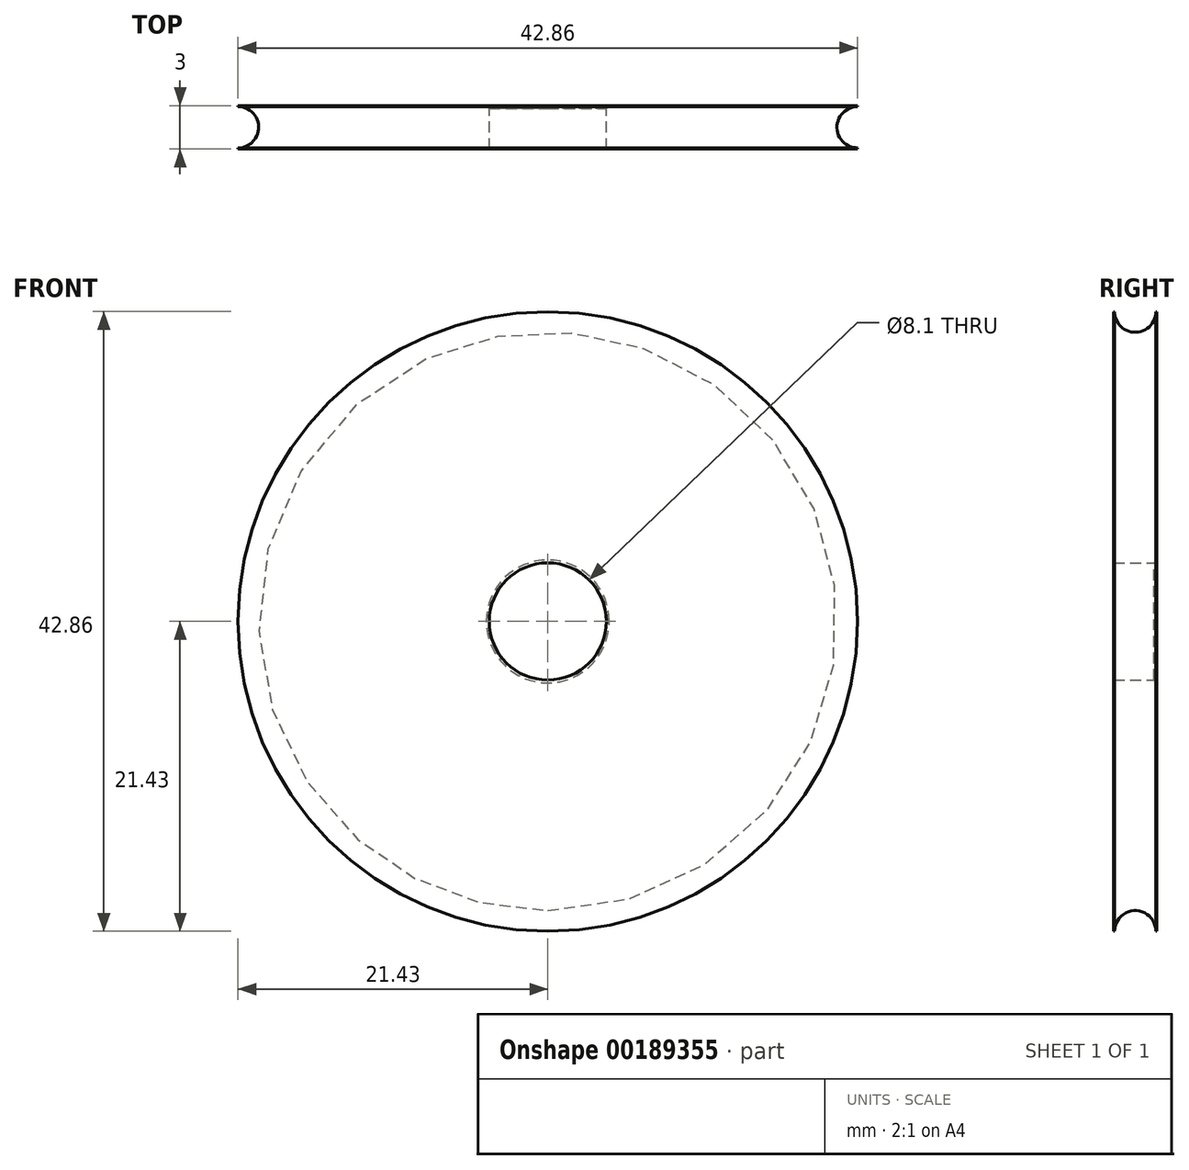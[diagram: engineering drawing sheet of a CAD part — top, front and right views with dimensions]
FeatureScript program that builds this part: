
annotation { "Feature Type Name" : "Feature", "Feature Type Description" : "" }
export const myFeature = defineFeature(function(context is Context, id is Id, definition is map)
    precondition{}
    {
        {
            var Q0;
            Q0=qCreatedBy(makeId("Front.planeOp"),FACE);
            var sketch = newSketch(context, id + "F0", { "sketchPlane" : qUnion([Q0])});
            skCircle(sketch, "E0", {"center": v(0, 0) * mm, "radius": 21.43 * mm});
            skCircle(sketch, "E1", {"center": v(0, 0) * mm, "radius": 4.05 * mm});
            skSolve(sketch);
        }
        {
            var Q0;
            Q0=makeQuery(id+"F0.imprint","IMPRINT",FACE,{"disambiguationData":[TD([[makeQuery(id+"F0.imprint","IMPRINT",EDGE,{"derivedFrom":sQuery(id+"F0.wireOp",EDGE,"E0")}),1.0]])]});
            extrude(context, id + "F1", {"entities" : qUnion([Q0]), "endBound" : BoundingType.SYMMETRIC, "depth" : 3 * mm});
        }
        {
            var Q0;
            Q0=qCreatedBy(makeId("Right.planeOp"),FACE);
            var sketch = newSketch(context, id + "F2", { "sketchPlane" : qUnion([Q0])});
            skLineSegment(sketch, "E2", {"start": v(0, 0) * mm, "end": v(0, 50.25) * mm});
            skLineSegment(sketch, "E3", {"start": v(1.43, 21.43) * mm, "end": v(-1.49, 21.43) * mm});
            skArc(sketch, "E4", {"start": v(-1.43, 21.43) * mm, "mid": v(0, 20) * mm, "end": v(1.43, 21.43) * mm});
            skLineSegment(sketch, "E5", {"start": v(1.43, 21.43) * mm, "end": v(1.5, 21.43) * mm});
            skLineSegment(sketch, "E6", {"start": v(0, 0) * mm, "end": v(-9.8, 0) * mm});
            skSolve(sketch);
        }
        {
            var Q0;
            Q0 = qSketchRegion(id + "F2", true);
            var Q1;
            Q1=sQuery(id+"F2.wireOp",EDGE,"E6");
            revolve(context, id + "F3", {"operationType" : NewBodyOperationType.REMOVE, "entities" : qUnion([Q0]), "axis" : qUnion([Q1]), "revolveType" : RevolveType.FULL, "oppositeDirection" : true});
        }
        {
            var Q0;
            Q0=makeQuery(id+"F1.opExtrude","CAP_EDGE",EDGE,{"disambiguationData":[OSD([sQuery(id+"F0.wireOp",EDGE,"E1")])],"isStart":true});
            chamfer(context, id + "F4", {"entities" : qUnion([Q0]), "width" : 0.2 * mm, "tangentPropagation" : true});
        }
    });
